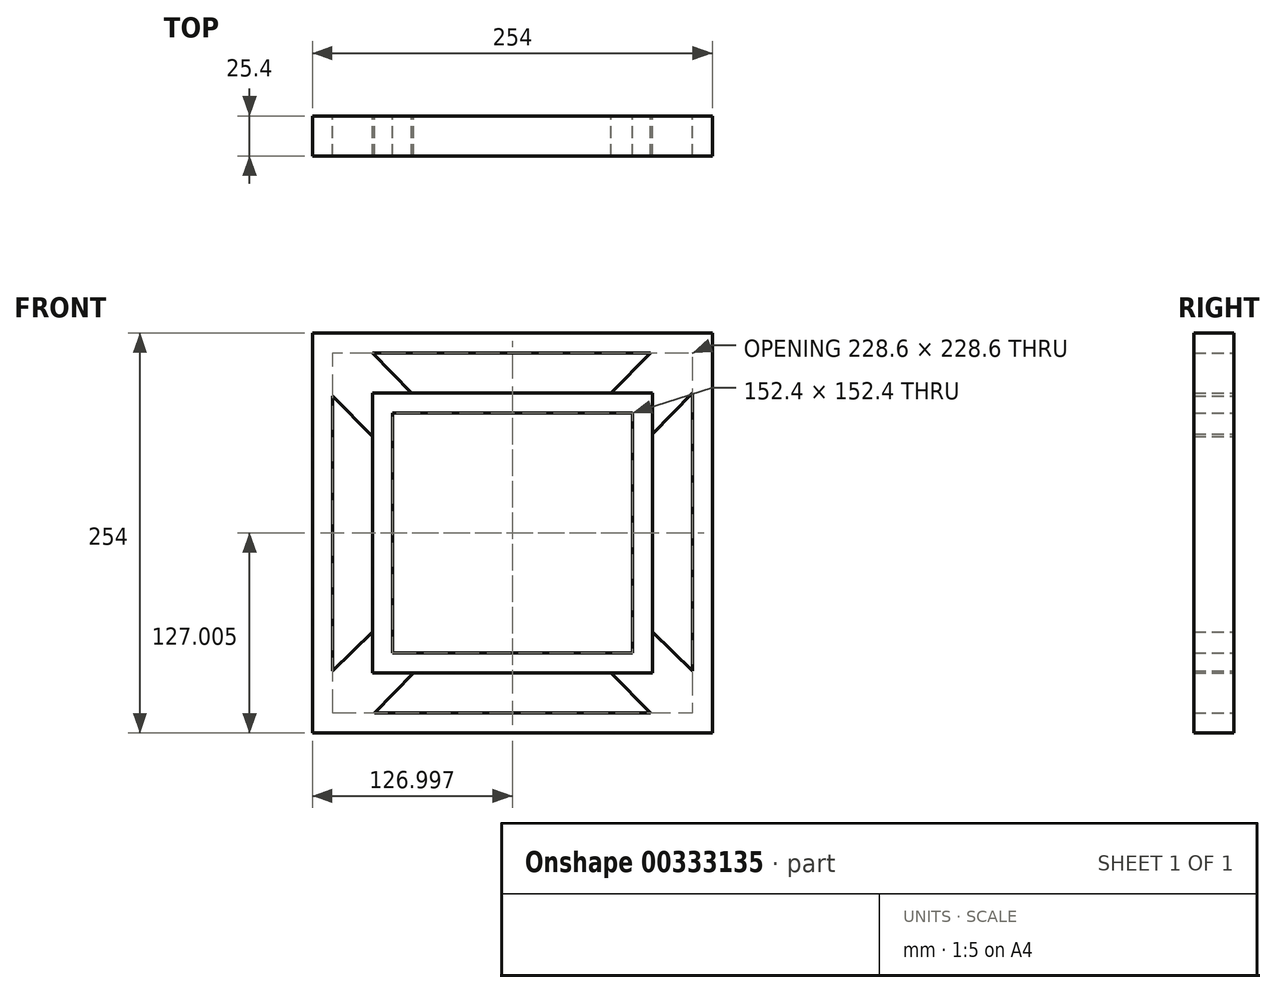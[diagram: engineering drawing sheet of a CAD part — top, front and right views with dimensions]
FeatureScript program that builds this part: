
annotation { "Feature Type Name" : "Feature", "Feature Type Description" : "" }
export const myFeature = defineFeature(function(context is Context, id is Id, definition is map)
    precondition{}
    {
        {
            var Q0;
            Q0=qCreatedBy(makeId("Front.planeOp"),FACE);
            var sketch = newSketch(context, id + "F0", { "sketchPlane" : qUnion([Q0])});
            skLineSegment(sketch, "E0.bottom", {"start": v(-189.74, 249.95) * mm, "end": v(64.26, 249.95) * mm});
            skLineSegment(sketch, "E0.top", {"start": v(-189.74, -4.05) * mm, "end": v(64.26, -4.05) * mm});
            skLineSegment(sketch, "E0.left", {"start": v(-189.74, 249.95) * mm, "end": v(-189.74, -4.05) * mm});
            skLineSegment(sketch, "E0.right", {"start": v(64.26, 249.95) * mm, "end": v(64.26, -4.05) * mm});
            skLineSegment(sketch, "E1.bottom", {"start": v(-177.04, 237.25) * mm, "end": v(51.56, 237.25) * mm});
            skLineSegment(sketch, "E1.top", {"start": v(-177.04, 8.65) * mm, "end": v(51.56, 8.65) * mm});
            skLineSegment(sketch, "E1.left", {"start": v(-177.04, 237.25) * mm, "end": v(-177.04, 8.65) * mm});
            skLineSegment(sketch, "E1.right", {"start": v(51.56, 237.25) * mm, "end": v(51.56, 8.65) * mm});
            skLineSegment(sketch, "E2.bottom", {"start": v(-151.64, 211.85) * mm, "end": v(26.16, 211.85) * mm});
            skLineSegment(sketch, "E2.top", {"start": v(-151.64, 34.05) * mm, "end": v(26.16, 34.05) * mm});
            skLineSegment(sketch, "E2.left", {"start": v(-151.64, 211.85) * mm, "end": v(-151.64, 34.05) * mm});
            skLineSegment(sketch, "E2.right", {"start": v(26.16, 211.85) * mm, "end": v(26.16, 34.05) * mm});
            skLineSegment(sketch, "E3.bottom", {"start": v(-138.94, 199.15) * mm, "end": v(13.46, 199.15) * mm});
            skLineSegment(sketch, "E3.top", {"start": v(-138.94, 46.75) * mm, "end": v(13.46, 46.75) * mm});
            skLineSegment(sketch, "E3.left", {"start": v(-138.94, 199.15) * mm, "end": v(-138.94, 46.75) * mm});
            skLineSegment(sketch, "E3.right", {"start": v(13.46, 199.15) * mm, "end": v(13.46, 46.75) * mm});
            skLineSegment(sketch, "E4", {"start": v(-177.04, 210.03) * mm, "end": v(-151.64, 184.11) * mm});
            skLineSegment(sketch, "E5", {"start": v(-151.64, 237.25) * mm, "end": v(-126.76, 211.85) * mm});
            skLineSegment(sketch, "E6", {"start": v(24.89, 237.25) * mm, "end": v(0, 211.85) * mm});
            skLineSegment(sketch, "E7", {"start": v(51.56, 211.85) * mm, "end": v(26.16, 185.93) * mm});
            skLineSegment(sketch, "E8", {"start": v(-151.64, 60.21) * mm, "end": v(-177.04, 35.32) * mm});
            skLineSegment(sketch, "E9", {"start": v(-125.49, 34.05) * mm, "end": v(-150.37, 8.65) * mm});
            skLineSegment(sketch, "E10", {"start": v(0, 34.05) * mm, "end": v(24.89, 8.65) * mm});
            skLineSegment(sketch, "E11", {"start": v(26.16, 60.21) * mm, "end": v(51.56, 35.32) * mm});
            skSolve(sketch);
        }
        {
            var Q0;
            Q0=makeQuery(id+"F0.imprint","IMPRINT",FACE,{"disambiguationData":[TD([[makeQuery(id+"F0.imprint","IMPRINT",EDGE,{"derivedFrom":sQuery(id+"F0.wireOp",EDGE,"E3.bottom")}),1.0]])]});
            var sketch = newSketch(context, id + "F1", { "sketchPlane" : qUnion([Q0])});
            skSolve(sketch);
        }
        {
            var Q0;
            Q0=makeQuery(id+"F1.imprint","IMPRINT",FACE,{"disambiguationData":[TD([[makeQuery(id+"F1.imprint","IMPRINT",EDGE,{"derivedFrom":makeQuery(id+"F0.imprint","IMPRINT",EDGE,{"derivedFrom":sQuery(id+"F0.wireOp",EDGE,"E3.bottom")})}),1.0]])]});
            var Q1;
            Q1=makeQuery(id+"F0.imprint","IMPRINT",FACE,{"disambiguationData":[TD([[makeQuery(id+"F0.imprint","IMPRINT",EDGE,{"derivedFrom":sQuery(id+"F0.wireOp",EDGE,"E0.bottom")}),-1.0]])]});
            var Q2;
            {var subQ3=sQuery(id+"F0.wireOp",EDGE,"E4");Q2=makeQuery(id+"F0.imprint","IMPRINT",FACE,{"disambiguationData":[TD([[makeQuery(id+"F0.imprint","IMPRINT",EDGE,{"derivedFrom":subQ3}),1.0]])]});}
            var Q3;
            {var subQ4=sQuery(id+"F0.wireOp",EDGE,"E6");Q3=makeQuery(id+"F0.imprint","IMPRINT",FACE,{"disambiguationData":[TD([[makeQuery(id+"F0.imprint","IMPRINT",EDGE,{"derivedFrom":subQ4}),1.0]])]});}
            var Q4;
            {var subQ4=sQuery(id+"F0.wireOp",EDGE,"E10");Q4=makeQuery(id+"F0.imprint","IMPRINT",FACE,{"disambiguationData":[TD([[makeQuery(id+"F0.imprint","IMPRINT",EDGE,{"derivedFrom":subQ4}),1.0]])]});}
            var Q5;
            {var subQ3=sQuery(id+"F0.wireOp",EDGE,"E8");Q5=makeQuery(id+"F0.imprint","IMPRINT",FACE,{"disambiguationData":[TD([[makeQuery(id+"F0.imprint","IMPRINT",EDGE,{"derivedFrom":subQ3}),1.0]])]});}
            extrude(context, id + "F2", {"entities" : qUnion([Q0, Q1, Q2, Q3, Q4, Q5]), "depth" : 25.4 * mm});
        }
    });
